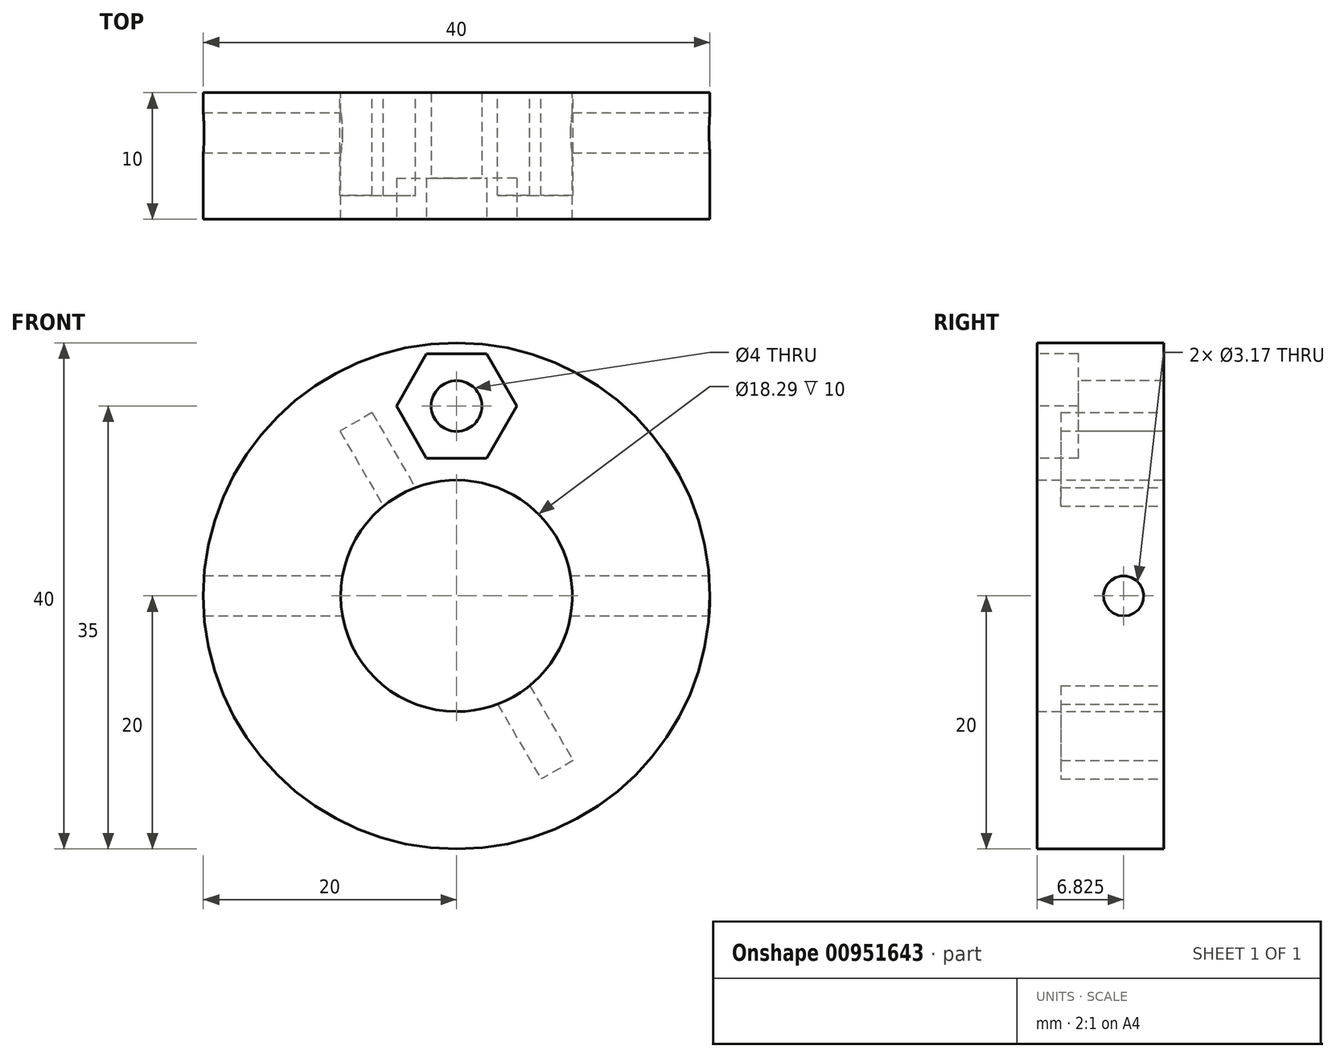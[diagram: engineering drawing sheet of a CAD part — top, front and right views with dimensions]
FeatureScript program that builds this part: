
annotation { "Feature Type Name" : "Feature", "Feature Type Description" : "" }
export const myFeature = defineFeature(function(context is Context, id is Id, definition is map)
    precondition{}
    {
        {
            var Q0;
            Q0=qCreatedBy(makeId("Front.planeOp"),FACE);
            var sketch = newSketch(context, id + "F0", { "sketchPlane" : qUnion([Q0])});
            skCircle(sketch, "E0", {"center": v(0, 0) * mm, "radius": 20 * mm});
            skSolve(sketch);
        }
        {
            var Q0;
            Q0=qSketchRegion(id+"F0",true);
            extrude(context, id + "F1", {"entities" : qUnion([Q0]), "depth" : 10 * mm, "offsetDistance" : 25 * mm});
        }
        {
            var Q0;
            Q0=makeQuery(id+"F1.opExtrude","CAP_FACE",FACE,{"disambiguationData":[OSD([sQuery(id+"F0.wireOp",EDGE,"E0")])],"isStart":true});
            var sketch = newSketch(context, id + "F2", { "sketchPlane" : qUnion([Q0])});
            skCircle(sketch, "E1.cCircle", {"center": v(0, 0) * mm, "radius": 5.75 * mm, "construction": true});
            skLineSegment(sketch, "E1.0", {"start": v(-3.32, 5.75) * mm, "end": v(3.32, 5.75) * mm});
            skLineSegment(sketch, "E1.1", {"start": v(3.32, 5.75) * mm, "end": v(6.64, 0) * mm});
            skLineSegment(sketch, "E1.2", {"start": v(6.64, 0) * mm, "end": v(3.32, -5.75) * mm});
            skLineSegment(sketch, "E1.3", {"start": v(3.32, -5.75) * mm, "end": v(-3.32, -5.75) * mm});
            skLineSegment(sketch, "E1.4", {"start": v(-3.32, -5.75) * mm, "end": v(-6.64, 0) * mm});
            skLineSegment(sketch, "E1.5", {"start": v(-6.64, 0) * mm, "end": v(-3.32, 5.75) * mm});
            skPoint(sketch, "E1.0.midPoint", {"position": v(0, 5.75) * mm});
            skSolve(sketch);
        }
        {
            var Q0;
            Q0=qSketchRegion(id+"F2",true);
            extrude(context, id + "F3", {"entities" : qUnion([Q0]), "operationType" : NewBodyOperationType.REMOVE, "oppositeDirection" : true, "depth" : 8.5 * mm, "offsetDistance" : 25 * mm});
        }
        {
            var Q0;
            Q0=makeQuery(id+"F1.opExtrude","CAP_FACE",FACE,{"disambiguationData":[OSD([sQuery(id+"F0.wireOp",EDGE,"E0")])],"isStart":false});
            var sketch = newSketch(context, id + "F4", { "sketchPlane" : qUnion([Q0])});
            skCircle(sketch, "E2", {"center": v(0, 15) * mm, "radius": 2 * mm});
            skSolve(sketch);
        }
        {
            var Q0;
            Q0=qSketchRegion(id+"F4",true);
            extrude(context, id + "F5", {"entities" : qUnion([Q0]), "operationType" : NewBodyOperationType.REMOVE, "endBound" : BoundingType.THROUGH_ALL, "oppositeDirection" : true, "depth" : 25 * mm, "offsetDistance" : 25 * mm});
        }
        {
            var Q0;
            Q0=makeQuery(id+"F1.opExtrude","CAP_FACE",FACE,{"disambiguationData":[OSD([sQuery(id+"F0.wireOp",EDGE,"E0")])],"isStart":false});
            var sketch = newSketch(context, id + "F6", { "sketchPlane" : qUnion([Q0])});
            skCircle(sketch, "E3.cCircle", {"center": v(0, 15) * mm, "radius": 4.11 * mm, "construction": true});
            skLineSegment(sketch, "E3.0", {"start": v(-2.38, 19.11) * mm, "end": v(2.37, 19.11) * mm});
            skLineSegment(sketch, "E3.1", {"start": v(2.37, 19.11) * mm, "end": v(4.75, 15) * mm});
            skLineSegment(sketch, "E3.2", {"start": v(4.75, 15) * mm, "end": v(2.38, 10.89) * mm});
            skLineSegment(sketch, "E3.3", {"start": v(2.38, 10.89) * mm, "end": v(-2.37, 10.89) * mm});
            skLineSegment(sketch, "E3.4", {"start": v(-2.37, 10.89) * mm, "end": v(-4.75, 15) * mm});
            skLineSegment(sketch, "E3.5", {"start": v(-4.75, 15) * mm, "end": v(-2.38, 19.11) * mm});
            skPoint(sketch, "E3.0.midPoint", {"position": v(0, 19.11) * mm});
            skSolve(sketch);
        }
        {
            var Q0;
            Q0=qSketchRegion(id+"F6",true);
            extrude(context, id + "F7", {"entities" : qUnion([Q0]), "operationType" : NewBodyOperationType.REMOVE, "oppositeDirection" : true, "depth" : 3.25 * mm, "offsetDistance" : 25 * mm});
        }
        {
            var Q0;
            Q0=makeQuery(id+"F1.opExtrude","CAP_FACE",FACE,{"disambiguationData":[OSD([sQuery(id+"F0.wireOp",EDGE,"E0")])],"isStart":false});
            var sketch = newSketch(context, id + "F8", { "sketchPlane" : qUnion([Q0])});
            skCircle(sketch, "E4", {"center": v(0, 0) * mm, "radius": 5.08 * mm});
            skSolve(sketch);
        }
        {
            var Q0;
            Q0=qSketchRegion(id+"F8",true);
            extrude(context, id + "F9", {"entities" : qUnion([Q0]), "operationType" : NewBodyOperationType.REMOVE, "endBound" : BoundingType.THROUGH_ALL, "oppositeDirection" : true, "depth" : 25 * mm, "offsetDistance" : 25 * mm});
        }
        {
            var Q0;
            Q0=makeQuery(id+"F1.opExtrude","CAP_FACE",FACE,{"disambiguationData":[OSD([sQuery(id+"F0.wireOp",EDGE,"E0")])],"isStart":true});
            var sketch = newSketch(context, id + "F10", { "sketchPlane" : qUnion([Q0])});
            skCircle(sketch, "E5", {"center": v(0, 0) * mm, "radius": 9.14 * mm});
            skSolve(sketch);
        }
        {
            var Q0;
            Q0 = qSketchRegion(id + "F10", true);
            var Q1;
            Q1=makeQuery(id+"F3.boolean.opBoolean","COPY",FACE,{"derivedFrom":makeQuery(id+"F3.opExtrude","CAP_FACE",FACE,{"disambiguationData":[OSD([sQuery(id+"F2.wireOp",EDGE,"E1.0"),sQuery(id+"F2.wireOp",EDGE,"E1.1"),sQuery(id+"F2.wireOp",EDGE,"E1.2"),sQuery(id+"F2.wireOp",EDGE,"E1.3"),sQuery(id+"F2.wireOp",EDGE,"E1.4"),sQuery(id+"F2.wireOp",EDGE,"E1.5")])],"isStart":false})});
            extrude(context, id + "F11", {"entities" : qUnion([Q0]), "operationType" : NewBodyOperationType.REMOVE, "endBound" : BoundingType.THROUGH_ALL, "oppositeDirection" : true, "depth" : 25 * mm, "endBoundEntityFace" : qUnion([Q1]), "offsetDistance" : 25 * mm});
        }
        {
            var Q0;
            Q0=makeQuery(id+"F1.opExtrude","CAP_FACE",FACE,{"disambiguationData":[OSD([sQuery(id+"F0.wireOp",EDGE,"E0")])],"isStart":true});
            var sketch = newSketch(context, id + "F12", { "sketchPlane" : qUnion([Q0])});
            skLineSegment(sketch, "E6.bottom", {"start": v(6.67, 14.48) * mm, "end": v(9.2, 13.02) * mm});
            skLineSegment(sketch, "E6.top", {"start": v(-9.2, -13.02) * mm, "end": v(-6.67, -14.48) * mm});
            skLineSegment(sketch, "E6.left", {"start": v(6.67, 14.48) * mm, "end": v(-9.2, -13.02) * mm});
            skLineSegment(sketch, "E6.right", {"start": v(9.2, 13.02) * mm, "end": v(-6.67, -14.48) * mm});
            skPoint(sketch, "E6.middle", {"position": v(0, 0) * mm});
            skLineSegment(sketch, "E7", {"start": v(7.94, 13.75) * mm, "end": v(-7.94, -13.75) * mm, "construction": true});
            skSolve(sketch);
        }
        {
            var Q0;
            Q0 = qSketchRegion(id + "F12", true);
            extrude(context, id + "F13", {"entities" : qUnion([Q0]), "operationType" : NewBodyOperationType.REMOVE, "oppositeDirection" : true, "depth" : 8.13 * mm, "offsetDistance" : 25.4 * mm});
        }
        {
            var Q0;
            Q0=qCreatedBy(makeId("Right.planeOp"),FACE);
            var sketch = newSketch(context, id + "F14", { "sketchPlane" : qUnion([Q0])});
            skCircle(sketch, "E8", {"center": v(-3.18, 0) * mm, "radius": 1.59 * mm});
            skSolve(sketch);
        }
        {
            var Q0;
            Q0 = qSketchRegion(id + "F14", true);
            extrude(context, id + "F15", {"entities" : qUnion([Q0]), "operationType" : NewBodyOperationType.REMOVE, "endBound" : BoundingType.SYMMETRIC, "oppositeDirection" : true, "depth" : 50.8 * mm, "offsetDistance" : 25.4 * mm});
        }
    });
